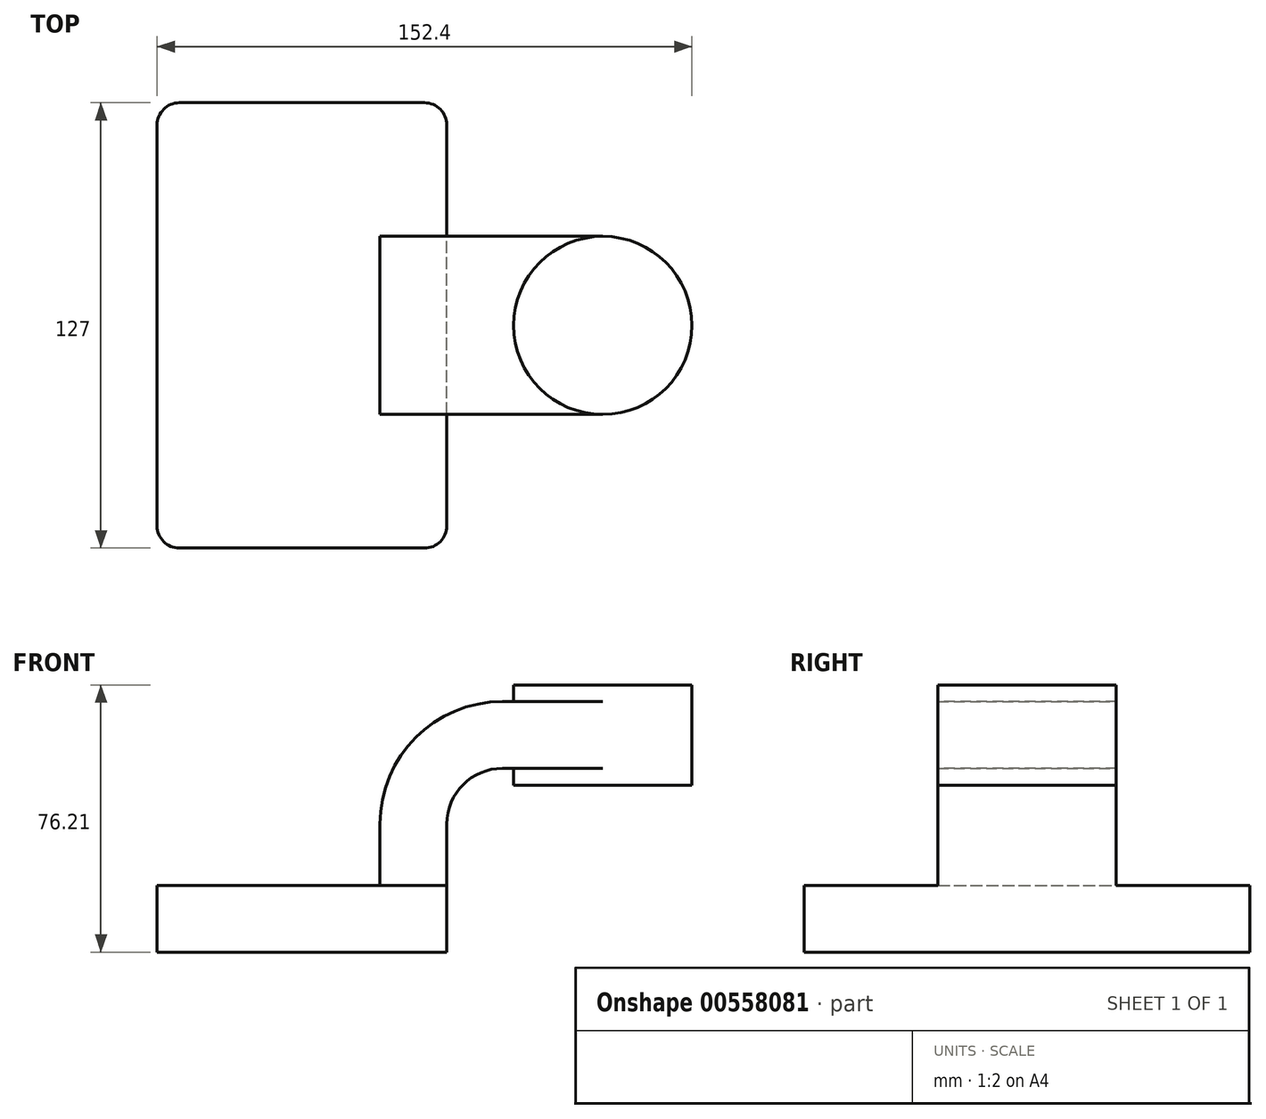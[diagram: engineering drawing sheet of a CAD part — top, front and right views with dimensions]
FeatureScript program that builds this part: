
annotation { "Feature Type Name" : "Feature", "Feature Type Description" : "" }
export const myFeature = defineFeature(function(context is Context, id is Id, definition is map)
    precondition{}
    {
        {
            var Q0;
            Q0=qCreatedBy(makeId("Front.planeOp"),FACE);
            var sketch = newSketch(context, id + "F0", { "sketchPlane" : qUnion([Q0])});
            skLineSegment(sketch, "E0.bottom", {"start": v(41.28, -9.52) * mm, "end": v(-41.28, -9.53) * mm});
            skLineSegment(sketch, "E0.top", {"start": v(41.28, 9.53) * mm, "end": v(-41.28, 9.53) * mm});
            skLineSegment(sketch, "E0.left", {"start": v(41.28, -9.52) * mm, "end": v(41.28, 9.53) * mm});
            skLineSegment(sketch, "E0.right", {"start": v(-41.28, -9.53) * mm, "end": v(-41.28, 9.53) * mm});
            skPoint(sketch, "E0.middle", {"position": v(0, 0) * mm});
            skLineSegment(sketch, "E1.bottom", {"start": v(111.12, 38.1) * mm, "end": v(60.33, 38.1) * mm});
            skLineSegment(sketch, "E1.top", {"start": v(111.12, 66.68) * mm, "end": v(60.33, 66.68) * mm});
            skLineSegment(sketch, "E1.left", {"start": v(111.12, 38.1) * mm, "end": v(111.12, 66.68) * mm});
            skLineSegment(sketch, "E1.right", {"start": v(60.33, 38.1) * mm, "end": v(60.33, 66.68) * mm});
            skPoint(sketch, "E1.middle", {"position": v(85.72, 52.39) * mm});
            skLineSegment(sketch, "E2", {"start": v(41.28, 9.53) * mm, "end": v(41.28, 27) * mm});
            skArc(sketch, "E3", {"start": v(41.27, 27) * mm, "mid": v(45.92, 38.23) * mm, "end": v(57.15, 42.88) * mm});
            skLineSegment(sketch, "E4", {"start": v(57.15, 42.88) * mm, "end": v(85.73, 42.88) * mm});
            skLineSegment(sketch, "E5.0", {"start": v(57.15, 61.93) * mm, "end": v(85.73, 61.93) * mm});
            skArc(sketch, "E5.1", {"start": v(22.22, 27) * mm, "mid": v(32.45, 51.7) * mm, "end": v(57.15, 61.93) * mm});
            skLineSegment(sketch, "E5.2", {"start": v(22.22, 9.53) * mm, "end": v(22.22, 27) * mm});
            skFitSpline(sketch, "E6", {"points": [v(-41.28, 9.53) * mm, v(57.15, 61.93) * mm], "startDerivative": vector(0.84, 143.03) * mm, "endDerivative": vector(141.42, -3) * mm});
            skLineSegment(sketch, "E7", {"start": v(85.73, 61.93) * mm, "end": v(85.73, 42.88) * mm});
            skLineSegment(sketch, "E8", {"start": v(85.73, 61.93) * mm, "end": v(85.72, 66.68) * mm});
            skLineSegment(sketch, "E9", {"start": v(85.73, 42.88) * mm, "end": v(85.73, 38.1) * mm});
            skSolve(sketch);
        }
        {
            var Q0;
            Q0=makeQuery(id+"F0.imprint","IMPRINT",FACE,{"disambiguationData":[TD([[makeQuery(id+"F0.imprint","IMPRINT",EDGE,{"derivedFrom":sQuery(id+"F0.wireOp",EDGE,"E0.bottom")}),-1.0]])]});
            extrude(context, id + "F1", {"entities" : qUnion([Q0]), "endBound" : BoundingType.SYMMETRIC, "depth" : 127 * mm, "offsetDistance" : 25.4 * mm});
        }
        {
            var Q0;
            {var subQ1=sQuery(id+"F0.wireOp",EDGE,"E2");Q0=makeQuery(id+"F0.imprint","IMPRINT",FACE,{"disambiguationData":[TD([[makeQuery(id+"F0.imprint","IMPRINT",EDGE,{"derivedFrom":subQ1}),1.0]])]});}
            var Q1;
            {var subQ5=sQuery(id+"F0.wireOp",EDGE,"E7");Q1=makeQuery(id+"F0.imprint","IMPRINT",FACE,{"disambiguationData":[TD([[makeQuery(id+"F0.imprint","IMPRINT",EDGE,{"derivedFrom":subQ5}),-1.0]])]});}
            extrude(context, id + "F2", {"entities" : qUnion([Q0, Q1]), "operationType" : NewBodyOperationType.ADD, "endBound" : BoundingType.SYMMETRIC, "depth" : 50.8 * mm, "offsetDistance" : 25.4 * mm});
        }
        {
            var Q0;
            Q0=makeQuery(id+"F0.imprint","IMPRINT",FACE,{"disambiguationData":[TD([[makeQuery(id+"F0.imprint","IMPRINT",EDGE,{"derivedFrom":sQuery(id+"F0.wireOp",EDGE,"E5.1")}),1.0]])]});
            extrude(context, id + "F3", {"entities" : qUnion([Q0]), "operationType" : NewBodyOperationType.ADD, "endBound" : BoundingType.SYMMETRIC, "depth" : 15.88 * mm, "offsetDistance" : 25.4 * mm});
        }
        {
            var Q0;
            {var subQ0=sQuery(id+"F0.wireOp",EDGE,"E1.left");Q0=makeQuery(id+"F0.imprint","IMPRINT",FACE,{"disambiguationData":[TD([[makeQuery(id+"F0.imprint","IMPRINT",EDGE,{"derivedFrom":subQ0}),1.0]])]});}
            var Q1;
            Q1=sQuery(id+"F0.wireOp",EDGE,"E7");
            revolve(context, id + "F4", {"operationType" : NewBodyOperationType.ADD, "entities" : qUnion([Q0]), "axis" : qUnion([Q1]), "revolveType" : RevolveType.FULL});
        }
        {
            var Q0;
            Q0=makeQuery(id+"F1.opExtrude","CAP_EDGE",EDGE,{"disambiguationData":[OSD([sQuery(id+"F0.wireOp",EDGE,"E0.left")])],"isStart":false});
            var Q1;
            Q1=makeQuery(id+"F1.opExtrude","CAP_EDGE",EDGE,{"disambiguationData":[OSD([sQuery(id+"F0.wireOp",EDGE,"E0.right")])],"isStart":false});
            var Q2;
            Q2=makeQuery(id+"F1.opExtrude","CAP_EDGE",EDGE,{"disambiguationData":[OSD([sQuery(id+"F0.wireOp",EDGE,"E0.right")])],"isStart":true});
            var Q3;
            Q3=makeQuery(id+"F1.opExtrude","CAP_EDGE",EDGE,{"disambiguationData":[OSD([sQuery(id+"F0.wireOp",EDGE,"E0.left")])],"isStart":true});
            fillet(context, id + "F5", {"entities" : qUnion([Q0, Q1, Q2, Q3]), "radius" : 6.35 * mm, "tangentPropagation" : true, "allowEdgeOverflow" : false});
        }
    });
